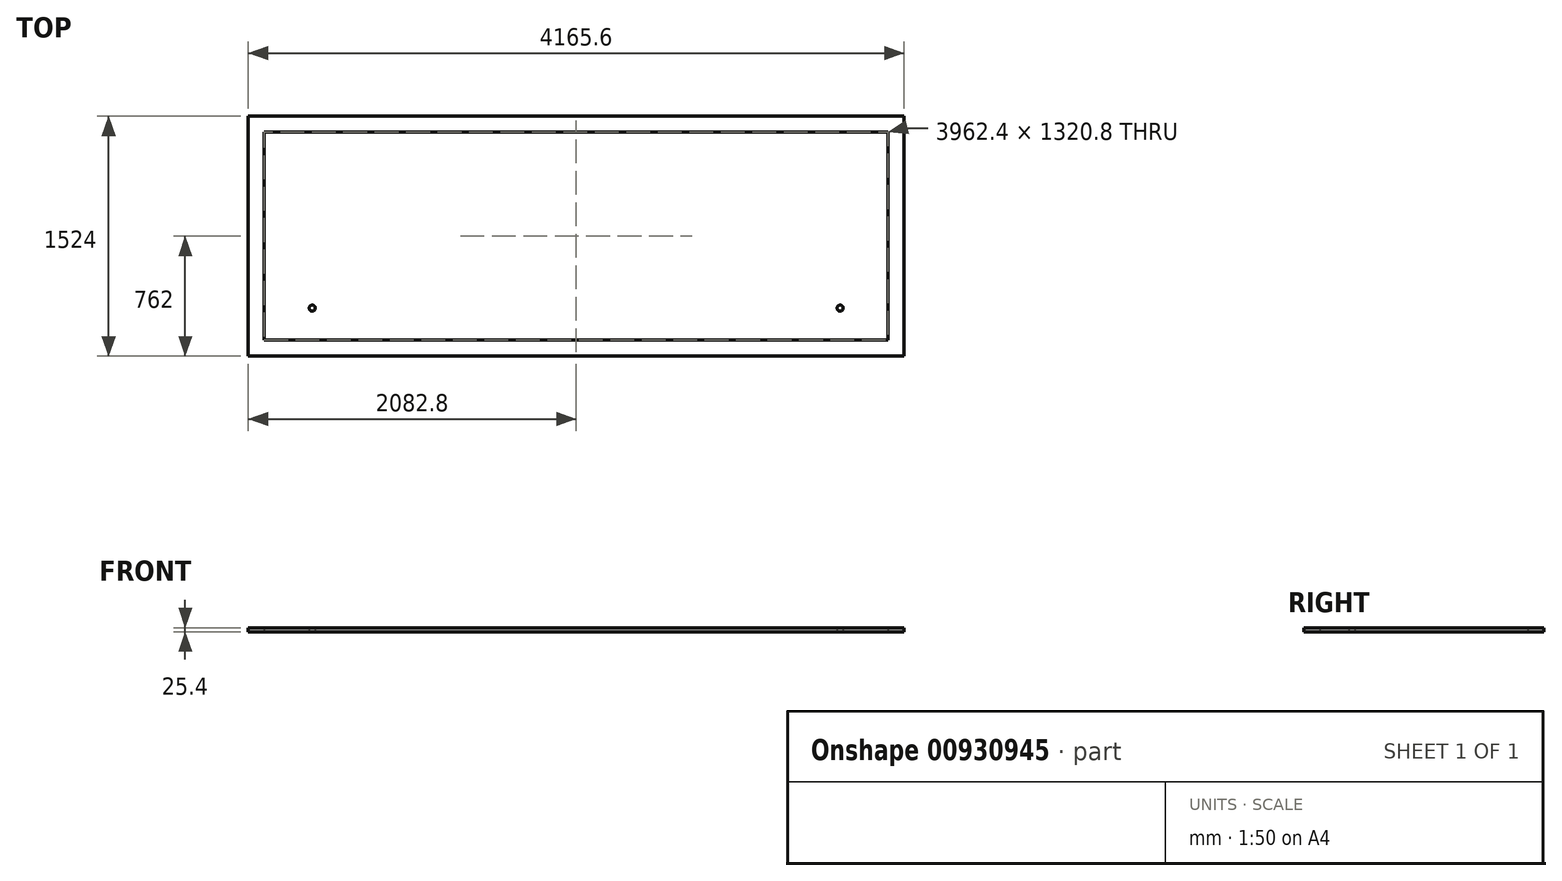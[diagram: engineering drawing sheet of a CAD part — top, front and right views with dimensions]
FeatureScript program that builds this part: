
annotation { "Feature Type Name" : "Feature", "Feature Type Description" : "" }
export const myFeature = defineFeature(function(context is Context, id is Id, definition is map)
    precondition{}
    {
        {
            var Q0;
            Q0=qCreatedBy(makeId("Top.planeOp"),FACE);
            var sketch = newSketch(context, id + "F0", { "sketchPlane" : qUnion([Q0])});
            skLineSegment(sketch, "E0.bottom", {"start": v(0, 0) * mm, "end": v(4165.6, 0) * mm});
            skLineSegment(sketch, "E0.top", {"start": v(0, -1524) * mm, "end": v(4165.6, -1524) * mm});
            skLineSegment(sketch, "E0.left", {"start": v(0, 0) * mm, "end": v(0, -1524) * mm});
            skLineSegment(sketch, "E0.right", {"start": v(4165.6, 0) * mm, "end": v(4165.6, -1524) * mm});
            skLineSegment(sketch, "E1.bottom", {"start": v(101.6, -101.6) * mm, "end": v(4064, -101.6) * mm});
            skLineSegment(sketch, "E1.top", {"start": v(101.6, -1422.4) * mm, "end": v(4064, -1422.4) * mm});
            skLineSegment(sketch, "E1.left", {"start": v(101.6, -101.6) * mm, "end": v(101.6, -1422.4) * mm});
            skLineSegment(sketch, "E1.right", {"start": v(4064, -101.6) * mm, "end": v(4064, -1422.4) * mm});
            skLineSegment(sketch, "E2.bottom", {"start": v(387.35, -101.6) * mm, "end": v(425.45, -101.6) * mm});
            skLineSegment(sketch, "E2.top", {"start": v(387.35, -1219.2) * mm, "end": v(425.45, -1219.2) * mm});
            skLineSegment(sketch, "E2.left", {"start": v(387.35, -101.6) * mm, "end": v(387.35, -1219.2) * mm});
            skLineSegment(sketch, "E2.right", {"start": v(425.45, -101.6) * mm, "end": v(425.45, -1219.2) * mm});
            skLineSegment(sketch, "E3.bottom", {"start": v(3740.15, -101.6) * mm, "end": v(3778.25, -101.6) * mm});
            skLineSegment(sketch, "E3.top", {"start": v(3740.15, -1219.2) * mm, "end": v(3778.25, -1219.2) * mm});
            skLineSegment(sketch, "E3.left", {"start": v(3740.15, -101.6) * mm, "end": v(3740.15, -1219.2) * mm});
            skLineSegment(sketch, "E3.right", {"start": v(3778.25, -101.6) * mm, "end": v(3778.25, -1219.2) * mm});
            skCircle(sketch, "E4", {"center": v(406.4, -1219.2) * mm, "radius": 19.05 * mm});
            skCircle(sketch, "E5", {"center": v(3759.2, -1219.2) * mm, "radius": 19.05 * mm});
            skSolve(sketch);
        }
        {
            var Q0;
            Q0=makeQuery(id+"F0.imprint","IMPRINT",FACE,{"disambiguationData":[TD([[makeQuery(id+"F0.imprint","IMPRINT",EDGE,{"derivedFrom":sQuery(id+"F0.wireOp",EDGE,"E0.bottom")}),-1.0]])]});
            var Q1;
            Q1=makeQuery(id+"F0.imprint","IMPRINT",FACE,{"disambiguationData":[TD([[makeQuery(id+"F0.imprint","IMPRINT",EDGE,{"derivedFrom":sQuery(id+"F0.wireOp",EDGE,"E2.bottom")}),-1.0]])]});
            var Q2;
            {var subQ0=sQuery(id+"F0.wireOp",EDGE,"E2.top");Q2=makeQuery(id+"F0.imprint","IMPRINT",FACE,{"disambiguationData":[TD([[makeQuery(id+"F0.imprint","IMPRINT",EDGE,{"derivedFrom":subQ0}),-1.0]])]});}
            var Q3;
            {var subQ0=sQuery(id+"F0.wireOp",EDGE,"E2.top");Q3=makeQuery(id+"F0.imprint","IMPRINT",FACE,{"disambiguationData":[TD([[makeQuery(id+"F0.imprint","IMPRINT",EDGE,{"derivedFrom":subQ0}),1.0]])]});}
            var Q4;
            Q4=makeQuery(id+"F0.imprint","IMPRINT",FACE,{"disambiguationData":[TD([[makeQuery(id+"F0.imprint","IMPRINT",EDGE,{"derivedFrom":sQuery(id+"F0.wireOp",EDGE,"E3.bottom")}),-1.0]])]});
            var Q5;
            {var subQ0=sQuery(id+"F0.wireOp",EDGE,"E3.top");Q5=makeQuery(id+"F0.imprint","IMPRINT",FACE,{"disambiguationData":[TD([[makeQuery(id+"F0.imprint","IMPRINT",EDGE,{"derivedFrom":subQ0}),1.0]])]});}
            var Q6;
            {var subQ0=sQuery(id+"F0.wireOp",EDGE,"E3.top");Q6=makeQuery(id+"F0.imprint","IMPRINT",FACE,{"disambiguationData":[TD([[makeQuery(id+"F0.imprint","IMPRINT",EDGE,{"derivedFrom":subQ0}),-1.0]])]});}
            extrude(context, id + "F1", {"entities" : qUnion([Q0, Q1, Q2, Q3, Q4, Q5, Q6]), "depth" : 25.4 * mm, "offsetDistance" : 25.4 * mm});
        }
    });
